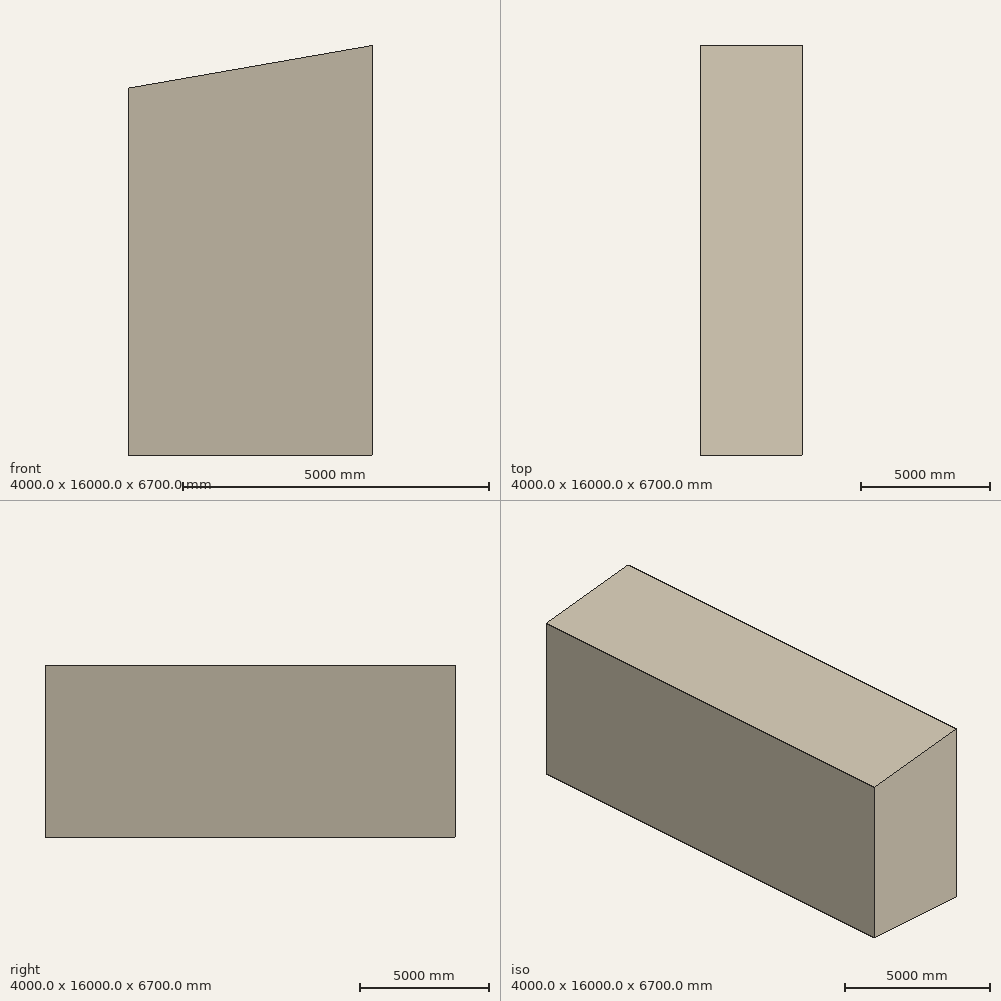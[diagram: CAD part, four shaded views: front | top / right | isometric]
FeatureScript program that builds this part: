
annotation { "Feature Type Name" : "Feature", "Feature Type Description" : "" }
export const myFeature = defineFeature(function(context is Context, id is Id, definition is map)
    precondition{}
    {
        {
            var Q0;
            Q0=qCreatedBy(makeId("Top.planeOp"),FACE);
            var sketch = newSketch(context, id + "F0", { "sketchPlane" : qUnion([Q0])});
            skLineSegment(sketch, "E0", {"start": v(224.55, 15886.35) * mm, "end": v(4224.55, 15886.35) * mm});
            skLineSegment(sketch, "E1", {"start": v(4224.55, 15886.35) * mm, "end": v(4224.55, -113.65) * mm});
            skLineSegment(sketch, "E2", {"start": v(4224.55, -113.65) * mm, "end": v(224.55, -113.65) * mm});
            skLineSegment(sketch, "E3", {"start": v(224.55, -113.65) * mm, "end": v(224.55, 15886.35) * mm});
            skSolve(sketch);
        }
        {
            var Q0;
            Q0=makeQuery(id+"F0.imprint","IMPRINT",FACE,{"disambiguationData":[TD([[makeQuery(id+"F0.imprint","IMPRINT",EDGE,{"derivedFrom":sQuery(id+"F0.wireOp",EDGE,"E0")}),-1.0]])]});
            extrude(context, id + "F1", {"entities" : qUnion([Q0]), "depth" : 6000 * mm});
        }
        {
            var Q0;
            Q0=makeQuery(id+"F1.opExtrude","SWEPT_FACE",FACE,{"disambiguationData":[OSD([sQuery(id+"F0.wireOp",EDGE,"E2")])]});
            var sketch = newSketch(context, id + "F2", { "sketchPlane" : qUnion([Q0])});
            skLineSegment(sketch, "E4", {"start": v(224.55, 6000) * mm, "end": v(4224.55, 6000) * mm});
            skLineSegment(sketch, "E5", {"start": v(4224.55, 6000) * mm, "end": v(4224.55, 6700) * mm});
            skLineSegment(sketch, "E6", {"start": v(4224.55, 6700) * mm, "end": v(224.55, 6000) * mm});
            skSolve(sketch);
        }
        {
            var Q0;
            Q0=makeQuery(id+"F2.imprint","IMPRINT",FACE,{"disambiguationData":[TD([[makeQuery(id+"F2.imprint","IMPRINT",EDGE,{"derivedFrom":sQuery(id+"F2.wireOp",EDGE,"E4")}),-1.0]])]});
            extrude(context, id + "F3", {"entities" : qUnion([Q0]), "operationType" : NewBodyOperationType.ADD, "oppositeDirection" : true, "depth" : 16000 * mm});
        }
        {
            var Q0;
            Q0=makeQuery(id+"F3.boolean.opBoolean","MERGE",FACE,{"derivedFrom":[makeQuery(id+"F1.opExtrude","SWEPT_FACE",FACE,{"disambiguationData":[OSD([sQuery(id+"F0.wireOp",EDGE,"E0")])]}),makeQuery(id+"F3.opExtrude","CAP_FACE",FACE,{"disambiguationData":[OSD([sQuery(id+"F2.wireOp",EDGE,"E4"),sQuery(id+"F2.wireOp",EDGE,"E5"),sQuery(id+"F2.wireOp",EDGE,"E6")])],"isStart":false})]});
            var Q1;
            Q1=makeQuery(id+"F1.opExtrude","CAP_FACE",FACE,{"disambiguationData":[OSD([sQuery(id+"F0.wireOp",EDGE,"E0"),sQuery(id+"F0.wireOp",EDGE,"E1"),sQuery(id+"F0.wireOp",EDGE,"E2"),sQuery(id+"F0.wireOp",EDGE,"E3")])],"isStart":true});
            shell(context, id + "F4", {"entities" : qUnion([Q0, Q1]), "thickness" : 2.5 * mm});
        }
    });
